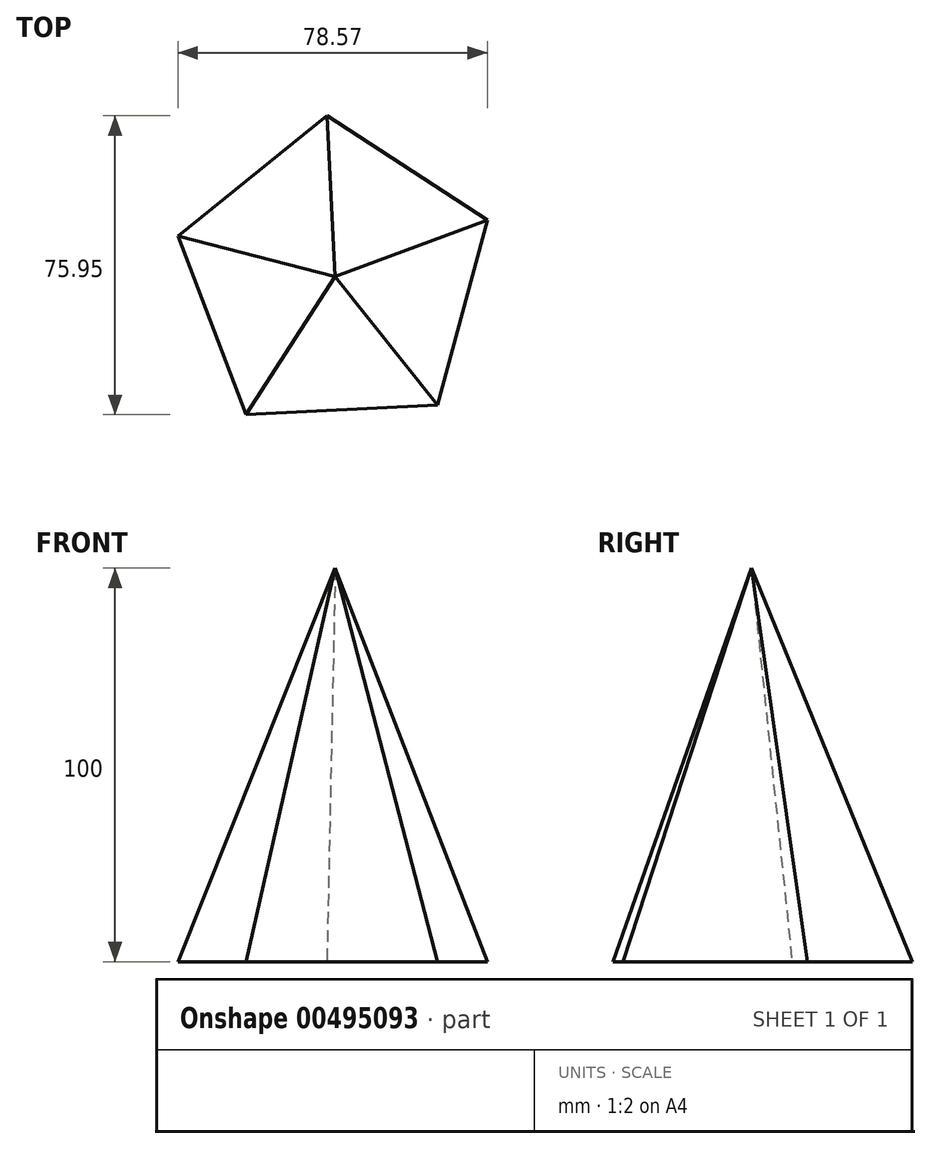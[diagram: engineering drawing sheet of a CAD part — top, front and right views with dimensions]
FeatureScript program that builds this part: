
annotation { "Feature Type Name" : "Feature", "Feature Type Description" : "" }
export const myFeature = defineFeature(function(context is Context, id is Id, definition is map)
    precondition{}
    {
        {
            var Q0;
            Q0=qCreatedBy(makeId("Top.planeOp"),FACE);
            var sketch = newSketch(context, id + "F0", { "sketchPlane" : qUnion([Q0])});
            skCircle(sketch, "E0.cCircle", {"center": v(0, -0.44) * mm, "radius": 41.36 * mm, "construction": true});
            skLineSegment(sketch, "E0.0", {"start": v(25.97, -32.63) * mm, "end": v(-22.6, -35.08) * mm});
            skLineSegment(sketch, "E0.1", {"start": v(-22.6, -35.08) * mm, "end": v(-39.93, 10.35) * mm});
            skLineSegment(sketch, "E0.2", {"start": v(-39.93, 10.35) * mm, "end": v(-2.08, 40.87) * mm});
            skLineSegment(sketch, "E0.3", {"start": v(-2.08, 40.87) * mm, "end": v(38.64, 14.3) * mm});
            skLineSegment(sketch, "E0.4", {"start": v(38.64, 14.3) * mm, "end": v(25.97, -32.63) * mm});
            skSolve(sketch);
        }
        {
            var Q0;
            Q0=qCreatedBy(makeId("Top.planeOp"),FACE);
            cPlane(context, id + "F1", {"entities" : qUnion([Q0]), "cplaneType" : CPlaneType.OFFSET, "offset" : 100 * mm, "width" : 152.4 * mm, "height" : 152.4 * mm});
        }
        {
            var Q0;
            Q0=qCreatedBy(id+"F1.planeOp",FACE);
            var sketch = newSketch(context, id + "F2", { "sketchPlane" : qUnion([Q0])});
            skPoint(sketch, "E1", {"position": v(0, 0) * mm});
            skSolve(sketch);
        }
        {
            var Q0;
            Q0=sQuery(id+"F2.wireOp",VERTEX,"E1");
            var Q1;
            Q1=makeQuery(id+"F0.imprint","IMPRINT",FACE,{"disambiguationData":[TD([[makeQuery(id+"F0.imprint","IMPRINT",EDGE,{"derivedFrom":sQuery(id+"F0.wireOp",EDGE,"E0.0")}),-1.0]])]});
            loft(context, id + "F3", {"sheetProfilesArray" : [{ "sheetProfileEntities" : qUnion([Q0]) }, { "sheetProfileEntities" : qUnion([Q1]) }]});
        }
    });
